# Revit family: ASP-B_BOTTOM
name_source: partatom
category: Mechanical Equipment
units: mm (PartAtom-declared; Revit-internal decimal feet)

## family parameters
Always vertical = Yes
Cut with Voids When Loaded = No
Part Type = Normal
Room Calculation Point = No
Round Connector Dimension = Use Diameter
Shared = No
Work Plane-Based = No

## types (6) — shared parameters
0 = 0' - 0"
1" = 0' - 1"
1.5 = 0' - 1 1/2"
2" = 0' - 2"
2' = 2' - 0"
4" = 0' - 4"
F = 0' - 3"
Manufacturer = Loren Cook Company
Model = ASP-B BOTTOM
ONE EIGTH = 0' - 0 1/8"
Type Comments = Air Supply Package Forward Curve Belt Drive Bottom Discharge Roof Mounted
URL = www.lorencook.com

## per-type parameters (varying)
| type | -(A/2) | -(C/2) | A | A/2 | B | B-C | B/2 | C | C/2 | D | E | H | H/2 | R_O | R_O/2 | T_SQ | T_SQ/2 | W | W/2 |
| 90_ASP-B_BOTTOM | -1' - 4 9/16" | -0' - 5 1/4" | 2' - 9 1/8" | 1' - 4 9/16" | 2' - 2 1/2" | 1' - 4" | 1' - 1 1/4" | 0' - 10 1/2" | 0' - 5 1/4" | 0' - 6 7/32" | 0' - 7" | 0' - 10 1/8" | 0' - 5 1/16" | 1' - 7 1/2" | 0' - 9 3/4" | 2' - 0 1/8" | 1' - 0 1/16" | 0' - 11 9/16" | 0' - 5 25/32" |
| 100_ASP-B_BOTTOM | -1' - 7 1/4" | -0' - 6 1/8" | 3' - 2 1/2" | 1' - 7 1/4" | 2' - 6" | 1' - 5 3/4" | 1' - 3" | 1' - 0 1/4" | 0' - 6 1/8" | 0' - 7 5/8" | 0' - 8 7/16" | 0' - 11 1/4" | 0' - 5 5/8" | 1' - 11 1/2" | 0' - 11 3/4" | 2' - 4 1/8" | 1' - 2 1/16" | 1' - 0 7/8" | 0' - 6 7/16" |
| 120_ASP-B_BOTTOM | -1' - 9 1/4" | -0' - 8 1/4" | 3' - 6 1/2" | 1' - 9 1/4" | 2' - 9 1/4" | 1' - 4 3/4" | 1' - 4 5/8" | 1' - 4 1/2" | 0' - 8 1/4" | 0' - 8 3/8" | 0' - 8 3/4" | 1' - 1 5/16" | 0' - 6 21/32" | 2' - 3 1/2" | 1' - 1 3/4" | 2' - 8 1/8" | 1' - 4 1/16" | 1' - 3 3/8" | 0' - 7 11/16" |
| 150_ASP-B_BOTTOM | -1' - 10 7/8" | -0' - 8 1/4" | 3' - 9 3/4" | 1' - 10 7/8" | 3' - 0 1/4" | 1' - 7 3/4" | 1' - 6 1/8" | 1' - 4 1/2" | 0' - 8 1/4" | 0' - 6 7/8" | 0' - 6 5/16" | 1' - 3 3/4" | 0' - 7 7/8" | 2' - 3 1/2" | 1' - 1 3/4" | 2' - 8 1/8" | 1' - 4 1/16" | 1' - 6 3/8" | 0' - 9 3/16" |
| 180_ASP-B_BOTTOM | -2' - 3 7/8" | -0' - 11 3/8" | 4' - 7 3/4" | 2' - 3 7/8" | 3' - 4 1/4" | 1' - 5 1/2" | 1' - 8 1/8" | 1' - 10 3/4" | 0' - 11 3/8" | 0' - 7 1/4" | 0' - 5 5/16" | 1' - 6 3/4" | 0' - 9 3/8" | 2' - 7 1/2" | 1' - 3 3/4" | 3' - 0 1/8" | 1' - 6 1/16" | 1' - 9 5/8" | 0' - 10 13/16" |
| 200_ASP-B_BOTTOM | -2' - 10" | -1' - 2 1/2" | 5' - 8" | 2' - 10" | 3' - 11 1/4" | 1' - 6 1/4" | 1' - 11 5/8" | 2' - 5" | 1' - 2 1/2" | 0' - 11 11/16" | 0' - 10 5/8" | 2' - 0 7/8" | 1' - 0 7/16" | 3' - 7 1/2" | 1' - 9 3/4" | 4' - 0 1/8" | 2' - 0 1/16" | 2' - 0 3/4" | 1' - 0 3/8" |

## geometry (parser evidence)
native form markers: Sweep x2
no freeform markers — native parametric forms only
